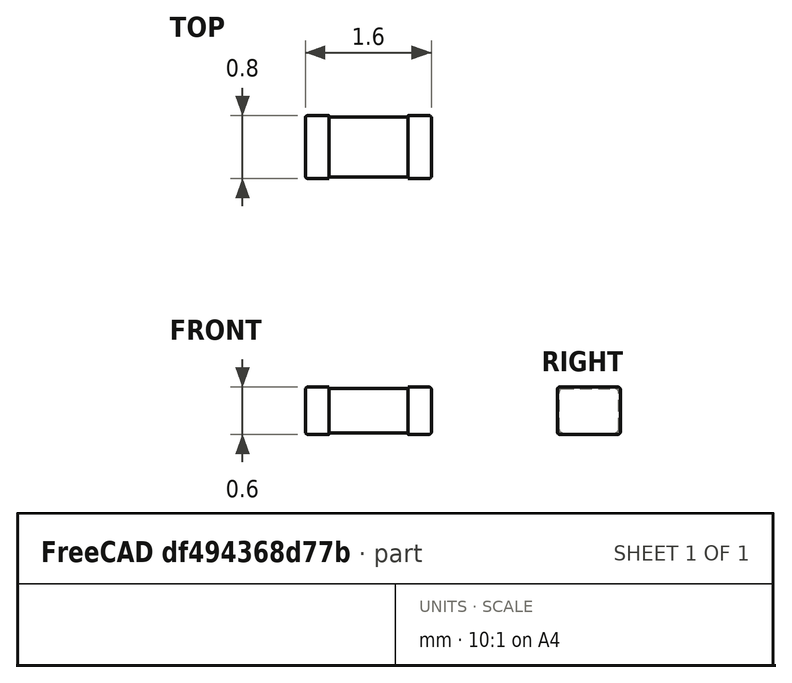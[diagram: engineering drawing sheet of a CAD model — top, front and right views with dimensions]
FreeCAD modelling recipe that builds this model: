
FCSTD DOCUMENT  (FreeCAD 0.16R6703 (Git))
Label: C_0603
License: All rights reserved
LicenseURL: http://en.wikipedia.org/wiki/All_rights_reserved
objects: Part::FeaturePython×4, Part::Box×2, Part::Fillet×2, Part::Mirroring×1, App::DocumentObjectGroup×1
note: 9 computed .brp shape members not serialized (recipe doc carries the construction recipe); baked Part::Feature solids carry a one-line shape summary decoded from their .brp

FEATURE [Part::Box] Box  label="Cube"
  Height = 0.56
  Length = 1
  Placement = pos=(-0.5,-0.38,0.02) rot=(0,0,1;0rad)
  Width = 0.76
FEATURE [Part::Fillet] Fillet  label="body-src"
  Base = -> Box
  Edges = 4 edges r=0.04: [Edge9,Edge10,Edge11,Edge12]
FEATURE [Part::Box] Box001  label="side-src"
  Height = 0.6
  Length = 0.3
  Placement = pos=(-0.8,-0.4,0) rot=(0,0,1;0rad)
  Width = 0.8
FEATURE [Part::Fillet] Fillet001  label="left-side-src"
  Base = -> Box001
  Edges = 8 edges r=0.03: [Edge1,Edge2,Edge3,Edge4,Edge9,Edge10,Edge11,Edge12]
FEATURE [Part::FeaturePython] Clone001  label="left-side-2"  # Draft clone (typed FeaturePython)
  Objects = -> [Fillet001]
  Scale = (1,1,1)
FEATURE [Part::Mirroring] Part__Mirroring  label="right-side-src"
  Base = (0,0,0)
  Normal = (1,0,0)
  Source = -> Clone001
FEATURE [App::DocumentObjectGroup] Group  label="src"
  Group = -> [Fillet,Box001,Fillet001,Part__Mirroring]
FEATURE [Part::FeaturePython] Clone  label="body"  # Draft clone (typed FeaturePython)
  Objects = -> [Fillet]
  Scale = (1,1,1)
FEATURE [Part::FeaturePython] Clone003  label="right-side"  # Draft clone (typed FeaturePython)
  Objects = -> [Part__Mirroring]
  Scale = (1,1,1)
FEATURE [Part::FeaturePython] Clone004  label="left-side"  # Draft clone (typed FeaturePython)
  Objects = -> [Clone001]
  Scale = (1,1,1)
